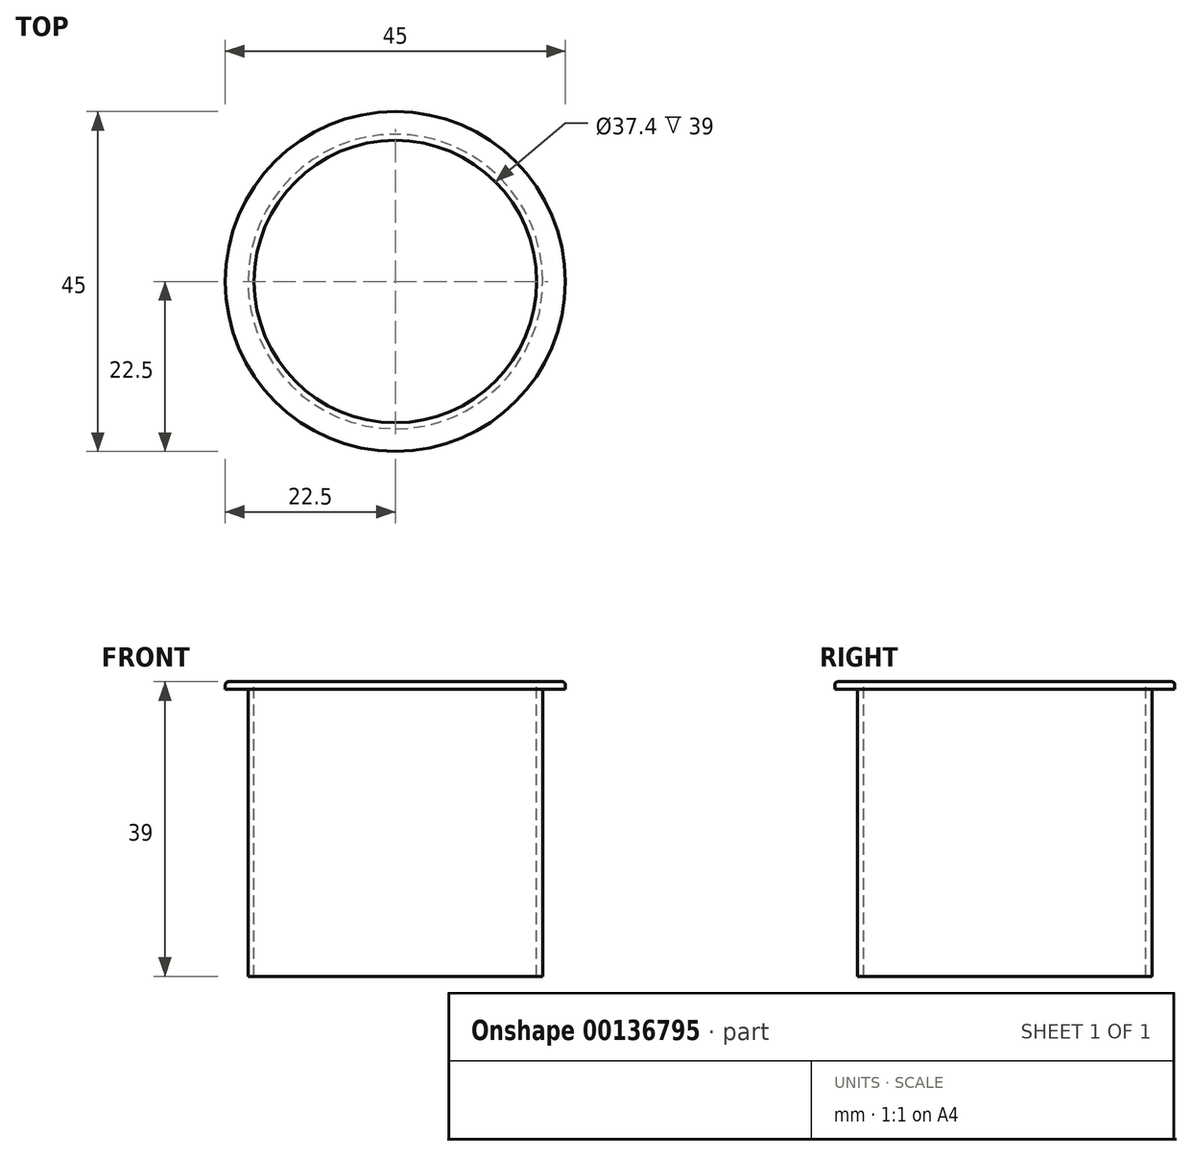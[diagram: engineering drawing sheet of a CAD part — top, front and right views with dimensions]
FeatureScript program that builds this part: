
annotation { "Feature Type Name" : "Feature", "Feature Type Description" : "" }
export const myFeature = defineFeature(function(context is Context, id is Id, definition is map)
    precondition{}
    {
        {
            var Q0;
            Q0=qCreatedBy(makeId("Top.planeOp"),FACE);
            var sketch = newSketch(context, id + "F0", { "sketchPlane" : qUnion([Q0])});
            skCircle(sketch, "E0", {"center": v(0, 0) * mm, "radius": 19.5 * mm});
            skCircle(sketch, "E1", {"center": v(0, 0) * mm, "radius": 22.5 * mm});
            skCircle(sketch, "E2", {"center": v(0, 0) * mm, "radius": 18.7 * mm});
            skSolve(sketch);
        }
        {
            var Q0;
            Q0=makeQuery(id+"F0.imprint","IMPRINT",FACE,{"disambiguationData":[TD([[makeQuery(id+"F0.imprint","IMPRINT",EDGE,{"derivedFrom":sQuery(id+"F0.wireOp",EDGE,"E0")}),1.0]])]});
            extrude(context, id + "F1", {"entities" : qUnion([Q0]), "oppositeDirection" : true, "depth" : 38 * mm});
        }
        {
            var Q0;
            Q0=makeQuery(id+"F0.imprint","IMPRINT",FACE,{"disambiguationData":[TD([[makeQuery(id+"F0.imprint","IMPRINT",EDGE,{"derivedFrom":sQuery(id+"F0.wireOp",EDGE,"E0")}),-1.0]])]});
            var Q1;
            Q1=makeQuery(id+"F0.imprint","IMPRINT",FACE,{"disambiguationData":[TD([[makeQuery(id+"F0.imprint","IMPRINT",EDGE,{"derivedFrom":sQuery(id+"F0.wireOp",EDGE,"E0")}),1.0]])]});
            extrude(context, id + "F2", {"entities" : qUnion([Q0, Q1]), "operationType" : NewBodyOperationType.ADD, "depth" : 1 * mm});
        }
        {
            var Q0;
            Q0=makeQuery(id+"F2.opExtrude","CAP_EDGE",EDGE,{"disambiguationData":[OSD([sQuery(id+"F0.wireOp",EDGE,"E1")])],"isStart":false});
            fillet(context, id + "F3", {"entities" : qUnion([Q0]), "radius" : .4 * mm, "tangentPropagation" : true, "allowEdgeOverflow" : false});
        }
    });
